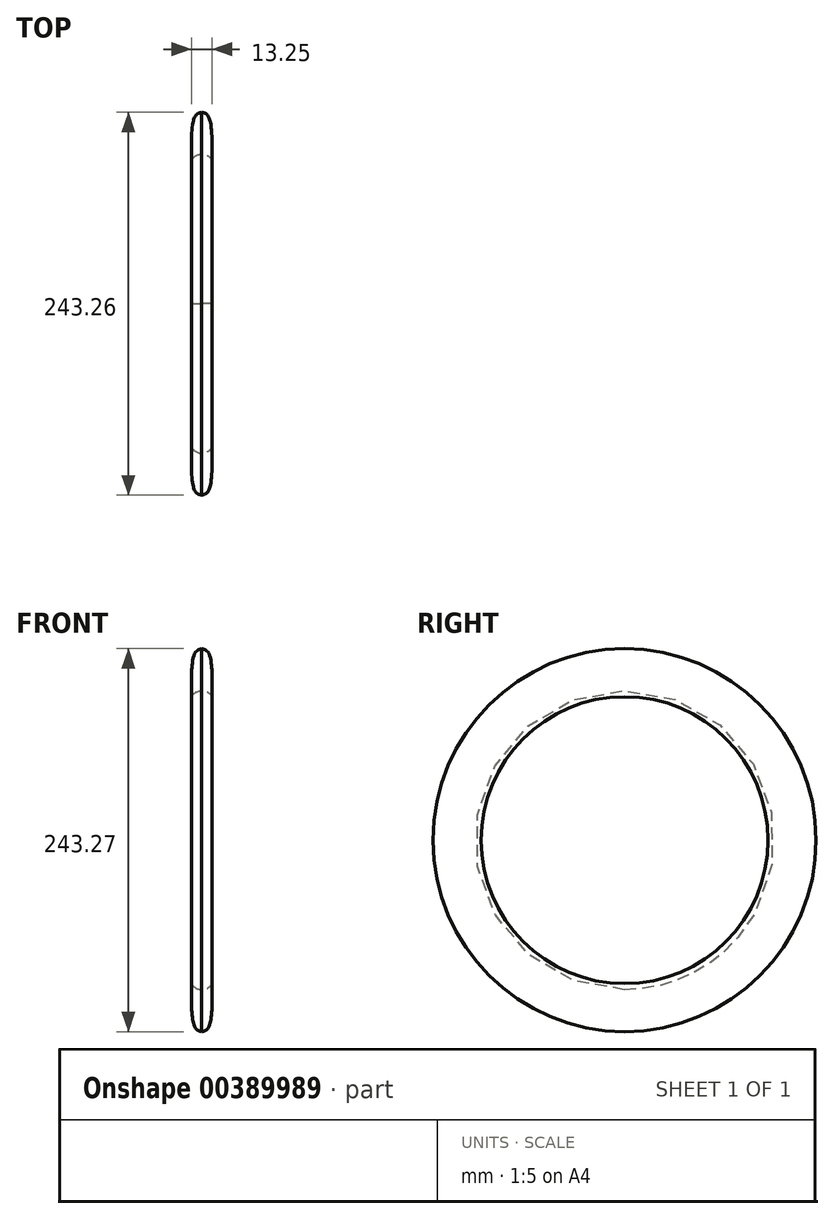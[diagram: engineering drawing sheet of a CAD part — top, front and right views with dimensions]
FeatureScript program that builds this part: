
annotation { "Feature Type Name" : "Feature", "Feature Type Description" : "" }
export const myFeature = defineFeature(function(context is Context, id is Id, definition is map)
    precondition{}
    {
        {
            var Q0;
            Q0=qCreatedBy(makeId("Front.planeOp"),FACE);
            var sketch = newSketch(context, id + "F0", { "sketchPlane" : qUnion([Q0])});
            skFitSpline(sketch, "E0", {"points": [v(-46.72, 5.66) * mm, v(-44.27, 33.74) * mm, v(-40.12, 36.2) * mm], "startDerivative": vector(-0.31, 50.76) * mm, "endDerivative": vector(15.73, 3.82) * mm});
            skFitSpline(sketch, "E1.MirrorCS", {"points": [v(-33.52, 5.66) * mm, v(-35.98, 33.74) * mm, v(-40.12, 36.2) * mm], "startDerivative": vector(0.31, 50.76) * mm, "endDerivative": vector(-15.73, 3.82) * mm});
            skArc(sketch, "E2", {"start": v(-33.52, 5.66) * mm, "mid": v(-40.12, 9.5) * mm, "end": v(-46.72, 5.66) * mm});
            skSolve(sketch);
        }
        {
            var Q0;
            Q0=qCreatedBy(makeId("Front.planeOp"),FACE);
            var sketch = newSketch(context, id + "F1", { "sketchPlane" : qUnion([Q0])});
            skLineSegment(sketch, "E3", {"start": v(152.21, -85.43) * mm, "end": v(-130.57, -85.43) * mm});
            skSolve(sketch);
        }
        {
            var Q0;
            Q0=makeQuery(id+"F0.imprint","IMPRINT",FACE,{"disambiguationData":[TD([[makeQuery(id+"F0.imprint","IMPRINT",EDGE,{"derivedFrom":sQuery(id+"F0.wireOp",EDGE,"E0")}),-1.0]])]});
            var Q1;
            Q1=sQuery(id+"F1.wireOp",EDGE,"E3");
            revolve(context, id + "F2", {"entities" : qUnion([Q0]), "axis" : qUnion([Q1]), "revolveType" : RevolveType.FULL});
        }
    });
